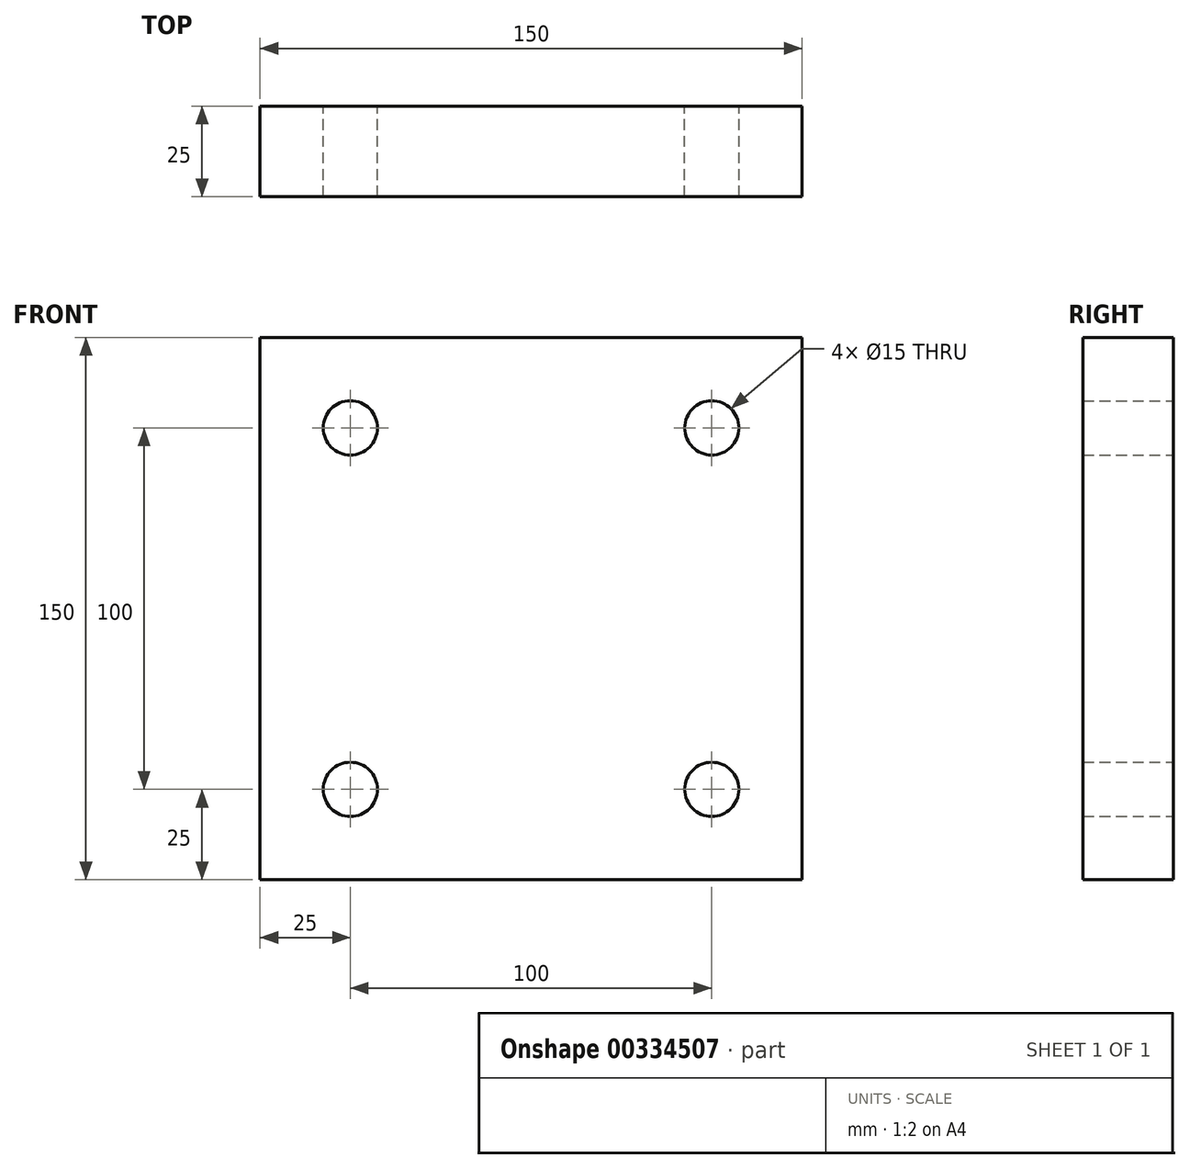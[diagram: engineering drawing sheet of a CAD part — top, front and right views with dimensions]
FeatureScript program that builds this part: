
annotation { "Feature Type Name" : "Feature", "Feature Type Description" : "" }
export const myFeature = defineFeature(function(context is Context, id is Id, definition is map)
    precondition{}
    {
        {
            var Q0;
            Q0=qCreatedBy(makeId("Front.planeOp"),FACE);
            var sketch = newSketch(context, id + "F0", { "sketchPlane" : qUnion([Q0])});
            skLineSegment(sketch, "E0.bottom", {"start": v(75, 75) * mm, "end": v(-75, 75) * mm});
            skLineSegment(sketch, "E0.top", {"start": v(75, -75) * mm, "end": v(-75, -75) * mm});
            skLineSegment(sketch, "E0.left", {"start": v(75, 75) * mm, "end": v(75, -75) * mm});
            skLineSegment(sketch, "E0.right", {"start": v(-75, 75) * mm, "end": v(-75, -75) * mm});
            skPoint(sketch, "E0.middle", {"position": v(0, 0) * mm});
            skLineSegment(sketch, "E1.bottom", {"start": v(50, 50) * mm, "end": v(-50, 50) * mm});
            skLineSegment(sketch, "E1.top", {"start": v(50, -50) * mm, "end": v(-50, -50) * mm});
            skLineSegment(sketch, "E1.left", {"start": v(50, 50) * mm, "end": v(50, -50) * mm});
            skLineSegment(sketch, "E1.right", {"start": v(-50, 50) * mm, "end": v(-50, -50) * mm});
            skPoint(sketch, "E2", {"position": v(-50, 50) * mm});
            skPoint(sketch, "E3", {"position": v(50, 50) * mm});
            skPoint(sketch, "E4", {"position": v(50, -50) * mm});
            skPoint(sketch, "E5", {"position": v(-50, -50) * mm});
            skCircle(sketch, "E6", {"center": v(-50, 50) * mm, "radius": 7.5 * mm});
            skCircle(sketch, "E7", {"center": v(50, 50) * mm, "radius": 7.5 * mm});
            skCircle(sketch, "E8", {"center": v(50, -50) * mm, "radius": 7.5 * mm});
            skCircle(sketch, "E9", {"center": v(-50, -50) * mm, "radius": 7.5 * mm});
            skSolve(sketch);
        }
        {
            var Q0;
            Q0 = qSketchRegion(id + "F0", true);
            var Q1;
            {var subQ5=sQuery(id+"F0.wireOp",EDGE,"E7");var subQ13=sQuery(id+"F0.wireOp",EDGE,"E1.bottom");var subQ14=makeQuery(id+"F0.imprint","INTERSECT",VERTEX,{"derivedFrom":[subQ13,subQ5]});Q1=makeQuery(id+"F0.imprint","IMPRINT",FACE,{"disambiguationData":[TD([[makeQuery(id+"F0.imprint","IMPRINT",EDGE,{"disambiguationData":[TD([[subQ14,-1.0]])],"derivedFrom":subQ13}),1.0]])]});}
            extrude(context, id + "F1", {"entities" : qUnion([Q0, Q1]), "depth" : 25 * mm});
        }
    });
